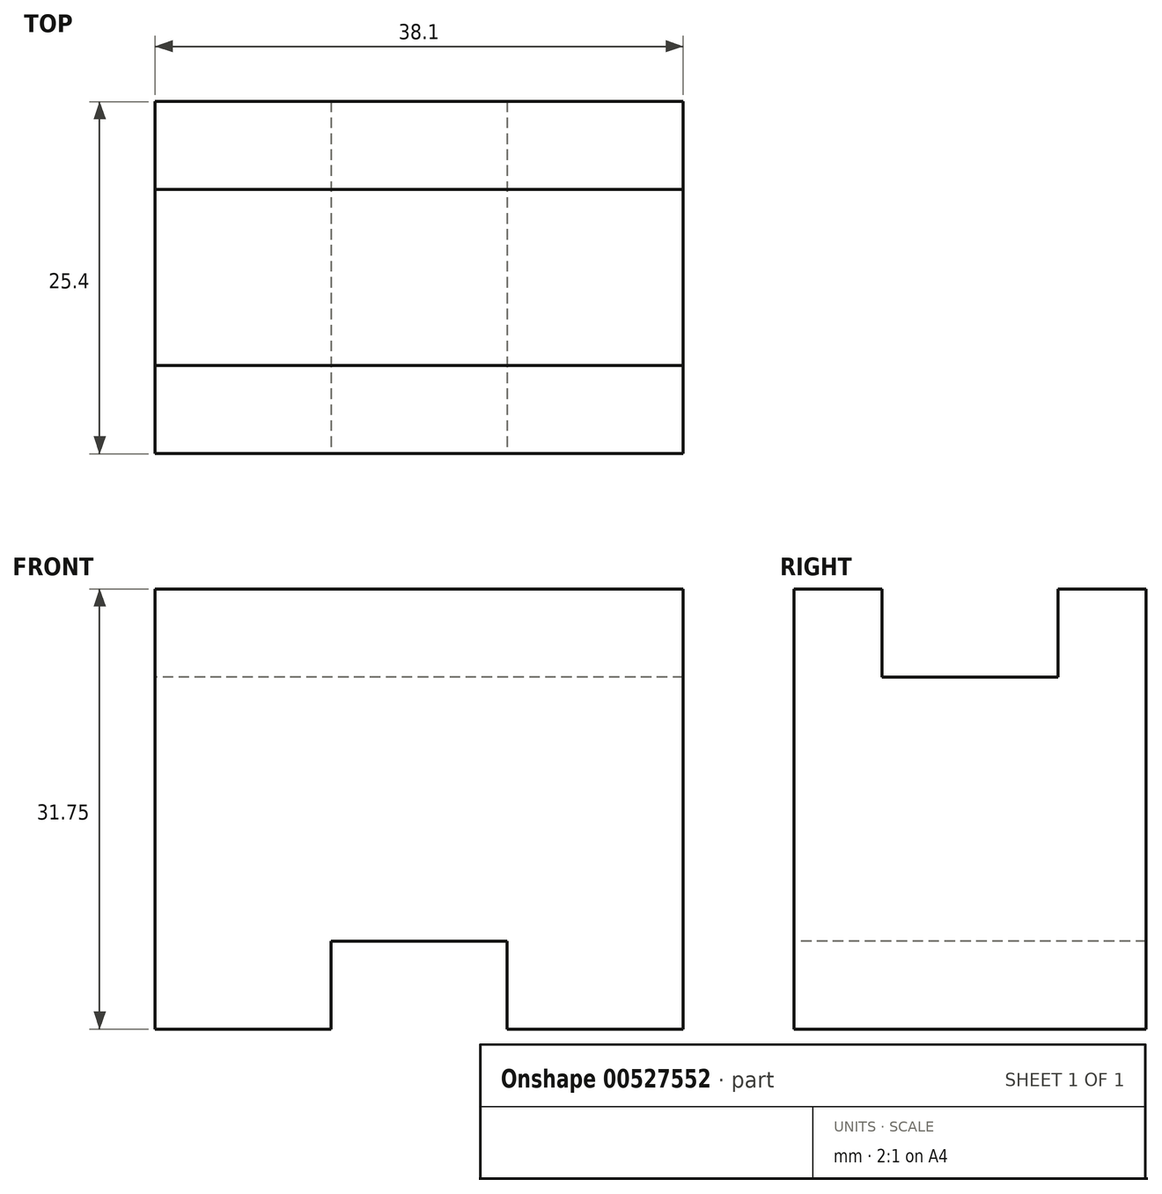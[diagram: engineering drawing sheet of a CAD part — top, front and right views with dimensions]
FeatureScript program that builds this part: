
annotation { "Feature Type Name" : "Feature", "Feature Type Description" : "" }
export const myFeature = defineFeature(function(context is Context, id is Id, definition is map)
    precondition{}
    {
        {
            var Q0;
            Q0=qCreatedBy(makeId("Right.planeOp"),FACE);
            var sketch = newSketch(context, id + "F0", { "sketchPlane" : qUnion([Q0])});
            skLineSegment(sketch, "E0", {"start": v(4.76, 0) * mm, "end": v(4.76, 31.75) * mm});
            skLineSegment(sketch, "E1", {"start": v(4.76, 31.75) * mm, "end": v(11.11, 31.75) * mm});
            skLineSegment(sketch, "E2", {"start": v(11.11, 31.75) * mm, "end": v(11.11, 25.4) * mm});
            skLineSegment(sketch, "E3", {"start": v(11.11, 25.4) * mm, "end": v(23.81, 25.4) * mm});
            skLineSegment(sketch, "E4", {"start": v(23.81, 25.4) * mm, "end": v(23.81, 31.75) * mm});
            skLineSegment(sketch, "E5", {"start": v(23.81, 31.75) * mm, "end": v(30.16, 31.75) * mm});
            skLineSegment(sketch, "E6", {"start": v(30.16, 31.75) * mm, "end": v(30.16, 0) * mm});
            skLineSegment(sketch, "E7", {"start": v(4.76, 0) * mm, "end": v(30.16, 0) * mm});
            skSolve(sketch);
        }
        {
            var Q0;
            Q0=makeQuery(id+"F0.imprint","IMPRINT",FACE,{"disambiguationData":[TD([[makeQuery(id+"F0.imprint","IMPRINT",EDGE,{"derivedFrom":sQuery(id+"F0.wireOp",EDGE,"E0")}),-1.0]])]});
            extrude(context, id + "F1", {"entities" : qUnion([Q0]), "depth" : 38.1 * mm, "offsetDistance" : 25.4 * mm});
        }
        {
            var Q0;
            Q0=makeQuery(id+"F1.opExtrude","SWEPT_FACE",FACE,{"disambiguationData":[OSD([sQuery(id+"F0.wireOp",EDGE,"E0")])]});
            var sketch = newSketch(context, id + "F2", { "sketchPlane" : qUnion([Q0])});
            skLineSegment(sketch, "E8", {"start": v(12.7, 0) * mm, "end": v(12.7, 6.35) * mm});
            skLineSegment(sketch, "E9", {"start": v(12.7, 6.35) * mm, "end": v(25.4, 6.35) * mm});
            skLineSegment(sketch, "E10", {"start": v(25.4, 6.35) * mm, "end": v(25.4, 0) * mm});
            skLineSegment(sketch, "E11", {"start": v(12.7, 0) * mm, "end": v(0, 0) * mm});
            skLineSegment(sketch, "E12", {"start": v(25.4, 0) * mm, "end": v(38.1, 0) * mm});
            skSolve(sketch);
        }
        {
            var Q0;
            {var subQ0=sQuery(id+"F2.wireOp",EDGE,"E8");Q0=makeQuery(id+"F2.imprint","IMPRINT",FACE,{"disambiguationData":[TD([[makeQuery(id+"F2.imprint","IMPRINT",EDGE,{"derivedFrom":subQ0}),-1.0]])]});}
            extrude(context, id + "F3", {"entities" : qUnion([Q0]), "operationType" : NewBodyOperationType.REMOVE, "oppositeDirection" : true, "depth" : 25.4 * mm, "offsetDistance" : 25.4 * mm});
        }
    });
